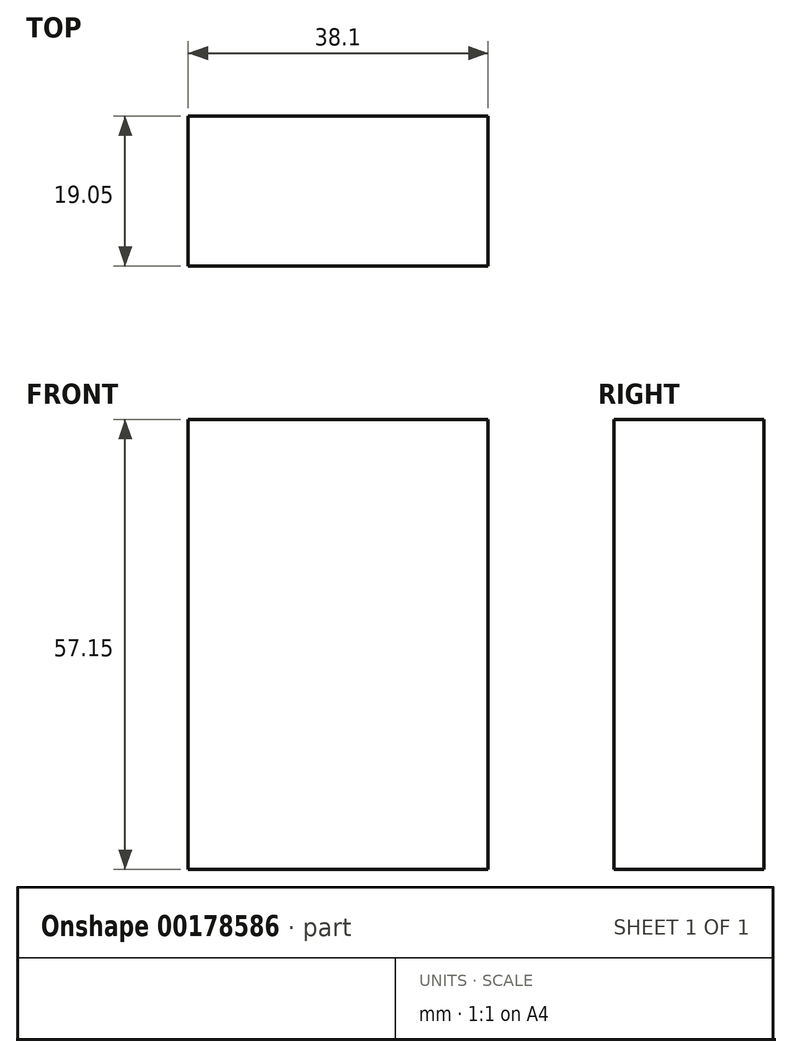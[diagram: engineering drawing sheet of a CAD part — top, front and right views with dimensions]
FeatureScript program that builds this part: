
annotation { "Feature Type Name" : "Feature", "Feature Type Description" : "" }
export const myFeature = defineFeature(function(context is Context, id is Id, definition is map)
    precondition{}
    {
        {
            var Q0;
            Q0=qCreatedBy(makeId("Front.planeOp"),FACE);
            var sketch = newSketch(context, id + "F0", { "sketchPlane" : qUnion([Q0])});
            skLineSegment(sketch, "E0", {"start": v(-56.45, 33.13) * mm, "end": v(-56.45, 14.08) * mm});
            skLineSegment(sketch, "E1", {"start": v(-56.45, 14.08) * mm, "end": v(-37.4, 14.08) * mm});
            skLineSegment(sketch, "E2", {"start": v(-37.4, 14.08) * mm, "end": v(-37.4, 33.13) * mm});
            skLineSegment(sketch, "E3", {"start": v(-37.4, 33.13) * mm, "end": v(-56.45, 33.13) * mm});
            skLineSegment(sketch, "E4", {"start": v(-56.45, -4.97) * mm, "end": v(-37.4, -4.97) * mm});
            skLineSegment(sketch, "E5", {"start": v(-37.4, -4.97) * mm, "end": v(-37.4, 14.08) * mm});
            skLineSegment(sketch, "E6", {"start": v(-56.45, 14.08) * mm, "end": v(-56.45, -4.97) * mm});
            skLineSegment(sketch, "E7", {"start": v(-56.45, -24.02) * mm, "end": v(-37.4, -24.02) * mm});
            skLineSegment(sketch, "E8", {"start": v(-37.4, -24.02) * mm, "end": v(-37.4, -4.97) * mm});
            skLineSegment(sketch, "E9", {"start": v(-56.45, -4.97) * mm, "end": v(-56.45, -24.02) * mm});
            skLineSegment(sketch, "E10", {"start": v(-37.4, 33.13) * mm, "end": v(-18.35, 33.13) * mm});
            skLineSegment(sketch, "E11", {"start": v(-18.35, 33.13) * mm, "end": v(-18.35, 14.08) * mm});
            skLineSegment(sketch, "E12", {"start": v(-18.35, 14.08) * mm, "end": v(-37.4, 14.08) * mm});
            skLineSegment(sketch, "E13", {"start": v(-18.35, 14.08) * mm, "end": v(-18.35, -4.97) * mm});
            skLineSegment(sketch, "E14", {"start": v(-18.35, -4.97) * mm, "end": v(-37.4, -4.97) * mm});
            skLineSegment(sketch, "E15", {"start": v(-18.35, -4.97) * mm, "end": v(-18.35, -24.02) * mm});
            skLineSegment(sketch, "E16", {"start": v(-18.35, -24.02) * mm, "end": v(-37.4, -24.02) * mm});
            skSolve(sketch);
        }
        {
            var Q0;
            Q0 = qSketchRegion(id + "F0", true);
            extrude(context, id + "F1", {"entities" : qUnion([Q0]), "depth" : 19.05 * mm});
        }
    });
